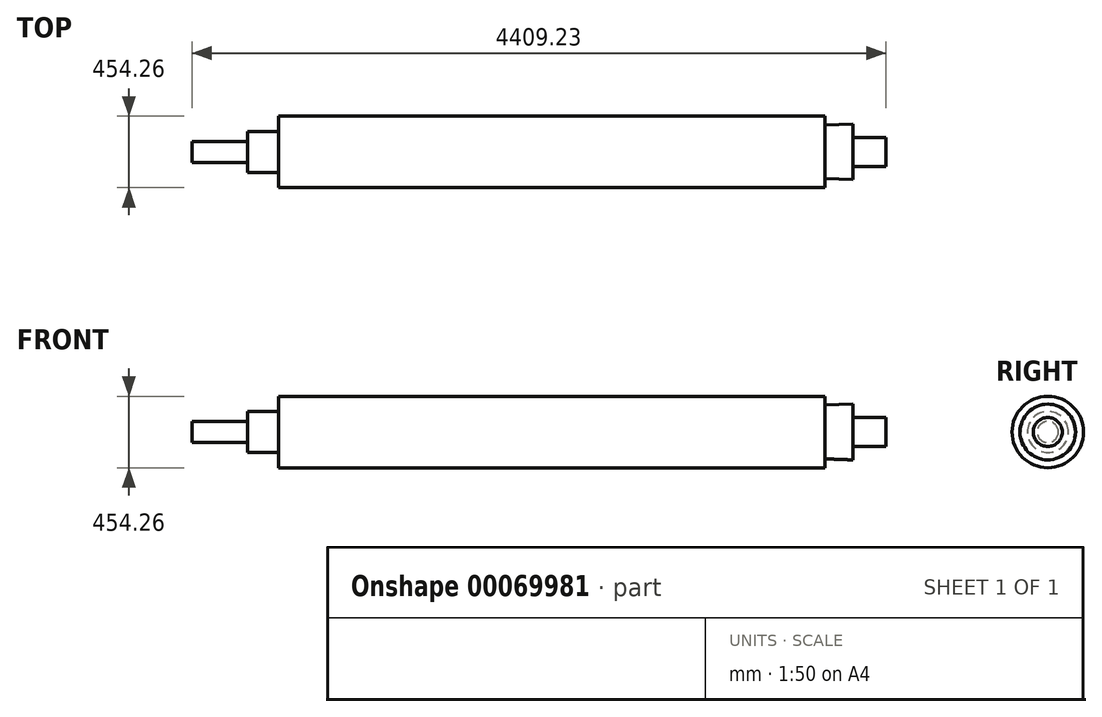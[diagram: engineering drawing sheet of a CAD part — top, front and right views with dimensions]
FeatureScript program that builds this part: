
annotation { "Feature Type Name" : "Feature", "Feature Type Description" : "" }
export const myFeature = defineFeature(function(context is Context, id is Id, definition is map)
    precondition{}
    {
        {
            var Q0;
            Q0=qCreatedBy(makeId("Top.planeOp"),FACE);
            var sketch = newSketch(context, id + "F1", { "sketchPlane" : qUnion([Q0])});
            skLineSegment(sketch, "E0.bottom", {"start": v(3085.58, -500) * mm, "end": v(585.58, -500) * mm});
            skLineSegment(sketch, "E0.top", {"start": v(3085.58, -484) * mm, "end": v(585.58, -484) * mm});
            skLineSegment(sketch, "E0.left", {"start": v(3085.58, -500) * mm, "end": v(3085.58, -484) * mm});
            skLineSegment(sketch, "E0.right", {"start": v(585.58, -500) * mm, "end": v(585.58, -484) * mm});
            skLineSegment(sketch, "E1", {"start": v(0, 0) * mm, "end": v(3158.39, 0) * mm, "construction": true});
            skLineSegment(sketch, "E2", {"start": v(-585.14, 0) * mm, "end": v(-585.14, -67.26) * mm});
            skLineSegment(sketch, "E3", {"start": v(-585.14, -67.26) * mm, "end": v(-232.1, -67.26) * mm});
            skLineSegment(sketch, "E4", {"start": v(-232.1, -67.26) * mm, "end": v(-232.1, -130.54) * mm});
            skLineSegment(sketch, "E5", {"start": v(-232.1, -130.54) * mm, "end": v(-35.6, -130.54) * mm});
            skLineSegment(sketch, "E6", {"start": v(-35.6, -130.54) * mm, "end": v(-35.6, -227.13) * mm});
            skLineSegment(sketch, "E7", {"start": v(-35.6, -227.13) * mm, "end": v(3436.42, -227.13) * mm});
            skLineSegment(sketch, "E8", {"start": v(3436.42, -227.13) * mm, "end": v(3436.42, -170.5) * mm});
            skLineSegment(sketch, "E9", {"start": v(3436.42, -170.5) * mm, "end": v(3612.38, -177.01) * mm});
            skLineSegment(sketch, "E10", {"start": v(3612.38, -177.01) * mm, "end": v(3612.38, -92.02) * mm});
            skLineSegment(sketch, "E11", {"start": v(3612.38, -92.02) * mm, "end": v(3824.1, -92.02) * mm});
            skLineSegment(sketch, "E12", {"start": v(3824.1, -92.02) * mm, "end": v(3824.1, 0) * mm});
            skLineSegment(sketch, "E13", {"start": v(3824.1, 0) * mm, "end": v(-585.14, 0) * mm});
            skSolve(sketch);
        }
        {
            var Q0;
            Q0=makeQuery(id+"F1.imprint","IMPRINT",FACE,{"disambiguationData":[TD([[makeQuery(id+"F1.imprint","IMPRINT",EDGE,{"derivedFrom":sQuery(id+"F1.wireOp",EDGE,"E2")}),1.0]])]});
            var Q1;
            Q1=sQuery(id+"F1.wireOp",EDGE,"E13");
            revolve(context, id + "F0", {"entities" : qUnion([Q0]), "axis" : qUnion([Q1]), "revolveType" : RevolveType.FULL});
        }
    });
